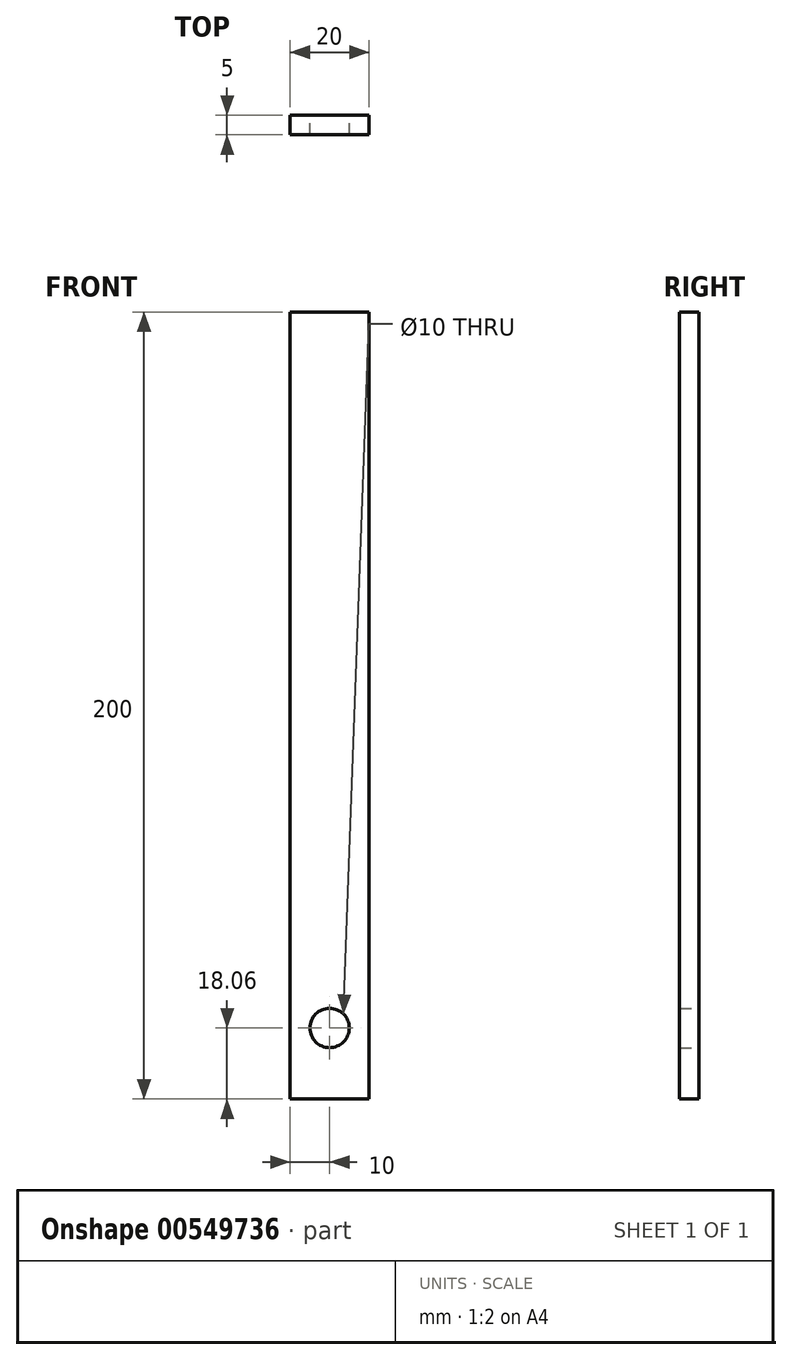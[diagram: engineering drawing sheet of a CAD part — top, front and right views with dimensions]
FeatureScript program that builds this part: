
annotation { "Feature Type Name" : "Feature", "Feature Type Description" : "" }
export const myFeature = defineFeature(function(context is Context, id is Id, definition is map)
    precondition{}
    {
        {
            var Q0;
            Q0=qCreatedBy(makeId("Front.planeOp"),FACE);
            var sketch = newSketch(context, id + "F0", { "sketchPlane" : qUnion([Q0])});
            skLineSegment(sketch, "E0.bottom", {"start": v(0, 0) * mm, "end": v(20, 0) * mm});
            skLineSegment(sketch, "E0.top", {"start": v(0, 200) * mm, "end": v(20, 200) * mm});
            skLineSegment(sketch, "E0.left", {"start": v(0, 0) * mm, "end": v(0, 200) * mm});
            skLineSegment(sketch, "E0.right", {"start": v(20, 0) * mm, "end": v(20, 200) * mm});
            skLineSegment(sketch, "E1", {"start": v(10, 0) * mm, "end": v(10, 18.06) * mm, "construction": true});
            skCircle(sketch, "E2", {"center": v(10, 18.06) * mm, "radius": 5 * mm});
            skSolve(sketch);
        }
        {
            var Q0;
            Q0 = qSketchRegion(id + "F0", true);
            extrude(context, id + "F1", {"entities" : qUnion([Q0]), "depth" : 5 * mm, "offsetDistance" : 25 * mm});
        }
    });
